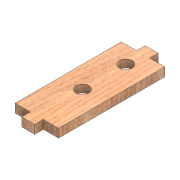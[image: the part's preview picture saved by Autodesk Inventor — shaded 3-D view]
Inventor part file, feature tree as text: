
AUTODESK INVENTOR PART (.ipt)
format: ipt  version: 2018 (Build 220112000, 112)  size: 150,016 bytes
history: native  units: mm
features: sketch x4, extrude x3, fillet x1
ambient origin geometry x8: Origin, YZ Plane, XZ Plane, XY Plane, X Axis, Y Axis, Z Axis, Center Point
bodies: Solid1 (feature_tree)
feature tree (8):
  extrude  "Extrusion1"  Depth=285.0mm
  extrude  "Extrusion2"  Depth=30.0mm
  extrude  "Extrusion3"  Depth=100.0mm
  sketch  "Sketch5"  dims[d10=20.0mm d11=0.0mm d13=125.0mm d14=30.0mm d19=10.0mm d20=0.0mm d21=100.0mm d22=135.0deg d23=142.5mm d24=3.0mm d26=35.0mm d27=20.0mm d28=20.0mm]
  fillet  "Fillet1"  Radius=100.0mm
  sketch  "Sketch1"  dims[d0=100.0mm d1=285.0mm]
  sketch  "Sketch2"  dims[d2=20.0mm d3=0.0mm d5=30.0mm]
  sketch  "Sketch3"  dims[d6=50.0mm d7=50.0mm d9=100.0mm]
